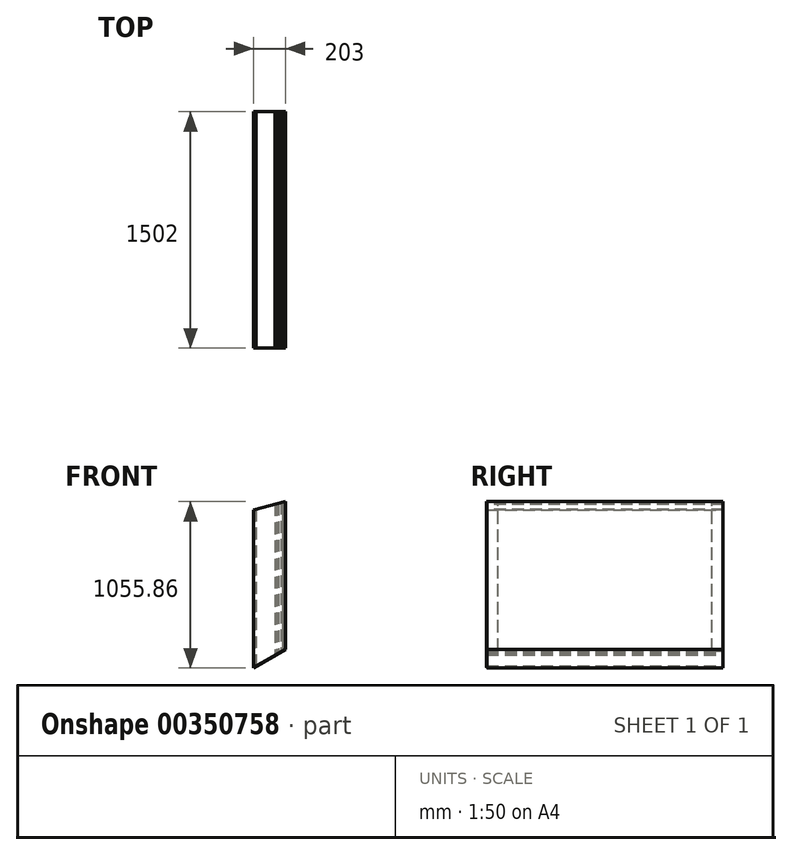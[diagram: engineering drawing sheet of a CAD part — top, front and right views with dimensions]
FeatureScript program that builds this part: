
annotation { "Feature Type Name" : "Feature", "Feature Type Description" : "" }
export const myFeature = defineFeature(function(context is Context, id is Id, definition is map)
    precondition{}
    {
        {
            var Q0;
            Q0=qCreatedBy(makeId("Right.planeOp"),FACE);
            var sketch = newSketch(context, id + "F0", { "sketchPlane" : qUnion([Q0])});
            skLineSegment(sketch, "E0", {"start": v(0, 0) * mm, "end": v(1500, 0) * mm});
            skLineSegment(sketch, "E1", {"start": v(1500, 0) * mm, "end": v(1500, 1200) * mm});
            skLineSegment(sketch, "E2", {"start": v(1500, 1200) * mm, "end": v(0, 1200) * mm});
            skLineSegment(sketch, "E3", {"start": v(0, 1200) * mm, "end": v(0, 0) * mm});
            skSolve(sketch);
        }
        {
            var Q0;
            Q0=makeQuery(id+"F0.imprint","IMPRINT",FACE,{"disambiguationData":[TD([[makeQuery(id+"F0.imprint","IMPRINT",EDGE,{"derivedFrom":sQuery(id+"F0.wireOp",EDGE,"E0")}),1.0]])]});
            extrude(context, id + "F1", {"entities" : qUnion([Q0]), "depth" : 6 * mm});
        }
        {
            var Q0;
            Q0=makeQuery(id+"F1.opExtrude","CAP_FACE",FACE,{"disambiguationData":[OSD([sQuery(id+"F0.wireOp",EDGE,"E0"),sQuery(id+"F0.wireOp",EDGE,"E1"),sQuery(id+"F0.wireOp",EDGE,"E2"),sQuery(id+"F0.wireOp",EDGE,"UxQu33BP-PdVc-IvKo-0Oal-Oq9sfbCTzBfW"),sQuery(id+"F0.wireOp",EDGE,"E3")])],"isStart":false});
            extrude(context, id + "F2", {"entities" : qUnion([Q0]), "depth" : 1 * mm});
        }
        {
            var Q0;
            Q0=makeQuery(id+"F2.opExtrude","CAP_FACE",FACE,{"disambiguationData":[OSD([sQuery(id+"F0.wireOp",EDGE,"E0"),sQuery(id+"F0.wireOp",EDGE,"E1"),sQuery(id+"F0.wireOp",EDGE,"E2"),sQuery(id+"F0.wireOp",EDGE,"UxQu33BP-PdVc-IvKo-0Oal-Oq9sfbCTzBfW"),sQuery(id+"F0.wireOp",EDGE,"E3")])],"isStart":false});
            extrude(context, id + "F3", {"entities" : qUnion([Q0]), "depth" : 10 * mm});
        }
        {
            var Q0;
            Q0=makeQuery(id+"F3.opExtrude","CAP_FACE",FACE,{"disambiguationData":[OSD([sQuery(id+"F0.wireOp",EDGE,"E0"),sQuery(id+"F0.wireOp",EDGE,"E1"),sQuery(id+"F0.wireOp",EDGE,"E2"),sQuery(id+"F0.wireOp",EDGE,"UxQu33BP-PdVc-IvKo-0Oal-Oq9sfbCTzBfW"),sQuery(id+"F0.wireOp",EDGE,"E3")])],"isStart":false});
            extrude(context, id + "F4", {"entities" : qUnion([Q0]), "depth" : 120 * mm});
        }
        {
            var Q0;
            Q0=makeQuery(id+"F4.opExtrude","CAP_FACE",FACE,{"disambiguationData":[OSD([sQuery(id+"F0.wireOp",EDGE,"E0"),sQuery(id+"F0.wireOp",EDGE,"E1"),sQuery(id+"F0.wireOp",EDGE,"E2"),sQuery(id+"F0.wireOp",EDGE,"UxQu33BP-PdVc-IvKo-0Oal-Oq9sfbCTzBfW"),sQuery(id+"F0.wireOp",EDGE,"E3")])],"isStart":false});
            extrude(context, id + "F5", {"entities" : qUnion([Q0]), "depth" : 10 * mm});
        }
        {
            var Q0;
            Q0=makeQuery(id+"F5.opExtrude","CAP_FACE",FACE,{"disambiguationData":[OSD([sQuery(id+"F0.wireOp",EDGE,"E0"),sQuery(id+"F0.wireOp",EDGE,"E1"),sQuery(id+"F0.wireOp",EDGE,"E2"),sQuery(id+"F0.wireOp",EDGE,"UxQu33BP-PdVc-IvKo-0Oal-Oq9sfbCTzBfW"),sQuery(id+"F0.wireOp",EDGE,"E3")])],"isStart":false});
            extrude(context, id + "F6", {"entities" : qUnion([Q0]), "depth" : 10 * mm});
        }
        {
            var Q0;
            Q0=makeQuery(id+"F6.opExtrude","CAP_FACE",FACE,{"disambiguationData":[OSD([sQuery(id+"F0.wireOp",EDGE,"E0"),sQuery(id+"F0.wireOp",EDGE,"E1"),sQuery(id+"F0.wireOp",EDGE,"E2"),sQuery(id+"F0.wireOp",EDGE,"UxQu33BP-PdVc-IvKo-0Oal-Oq9sfbCTzBfW"),sQuery(id+"F0.wireOp",EDGE,"E3")])],"isStart":false});
            extrude(context, id + "F7", {"entities" : qUnion([Q0]), "depth" : 18 * mm});
        }
        {
            var Q0;
            Q0=makeQuery(id+"F7.opExtrude","CAP_FACE",FACE,{"disambiguationData":[OSD([sQuery(id+"F0.wireOp",EDGE,"E0"),sQuery(id+"F0.wireOp",EDGE,"E1"),sQuery(id+"F0.wireOp",EDGE,"E2"),sQuery(id+"F0.wireOp",EDGE,"UxQu33BP-PdVc-IvKo-0Oal-Oq9sfbCTzBfW"),sQuery(id+"F0.wireOp",EDGE,"E3")])],"isStart":false});
            extrude(context, id + "F8", {"entities" : qUnion([Q0]), "depth" : 10 * mm});
        }
        {
            var Q0;
            Q0=makeQuery(id+"F8.opExtrude","CAP_FACE",FACE,{"disambiguationData":[OSD([sQuery(id+"F0.wireOp",EDGE,"E0"),sQuery(id+"F0.wireOp",EDGE,"E1"),sQuery(id+"F0.wireOp",EDGE,"E2"),sQuery(id+"F0.wireOp",EDGE,"E3")])],"isStart":false});
            extrude(context, id + "F9", {"entities" : qUnion([Q0]), "depth" : 1 * mm});
        }
        {
            var Q0;
            Q0=makeQuery(id+"F9.opExtrude","CAP_FACE",FACE,{"disambiguationData":[OSD([sQuery(id+"F0.wireOp",EDGE,"E0"),sQuery(id+"F0.wireOp",EDGE,"E1"),sQuery(id+"F0.wireOp",EDGE,"E2"),sQuery(id+"F0.wireOp",EDGE,"E3")])],"isStart":false});
            var sketch = newSketch(context, id + "F10", { "sketchPlane" : qUnion([Q0])});
            skLineSegment(sketch, "E4.bottom", {"start": v(0, 0) * mm, "end": v(70, 0) * mm});
            skLineSegment(sketch, "E4.top", {"start": v(0, 1200) * mm, "end": v(70, 1200) * mm});
            skLineSegment(sketch, "E4.left", {"start": v(0, 0) * mm, "end": v(0, 1200) * mm});
            skLineSegment(sketch, "E4.right", {"start": v(70, 0) * mm, "end": v(70, 1200) * mm});
            skLineSegment(sketch, "E5.bottom", {"start": v(1500, 0) * mm, "end": v(1430, 0) * mm});
            skLineSegment(sketch, "E5.top", {"start": v(1500, 1200) * mm, "end": v(1430, 1200) * mm});
            skLineSegment(sketch, "E5.left", {"start": v(1500, 0) * mm, "end": v(1500, 1200) * mm});
            skLineSegment(sketch, "E5.right", {"start": v(1430, 0) * mm, "end": v(1430, 1200) * mm});
            skSolve(sketch);
        }
        {
            var Q0;
            Q0=qSketchRegion(id+"F10",true);
            extrude(context, id + "F11", {"entities" : qUnion([Q0]), "depth" : 8 * mm});
        }
        {
            var Q0;
            Q0=makeQuery(id+"F11.opExtrude","CAP_FACE",FACE,{"disambiguationData":[OSD([sQuery(id+"F10.wireOp",EDGE,"E4.bottom"),sQuery(id+"F10.wireOp",EDGE,"E4.top"),sQuery(id+"F10.wireOp",EDGE,"E4.left"),sQuery(id+"F10.wireOp",EDGE,"E4.right")])],"isStart":false});
            var sketch = newSketch(context, id + "F12", { "sketchPlane" : qUnion([Q0])});
            skLineSegment(sketch, "E6.bottom", {"start": v(0, 0) * mm, "end": v(1500, 0) * mm});
            skLineSegment(sketch, "E6.top", {"start": v(0, 1200) * mm, "end": v(1500, 1200) * mm});
            skLineSegment(sketch, "E6.left", {"start": v(0, 0) * mm, "end": v(0, 1200) * mm});
            skLineSegment(sketch, "E6.right", {"start": v(1500, 0) * mm, "end": v(1500, 1200) * mm});
            skSolve(sketch);
        }
        {
            var Q0;
            Q0=qSketchRegion(id+"F12",true);
            extrude(context, id + "F13", {"entities" : qUnion([Q0]), "depth" : 8 * mm});
        }
        {
            var Q0;
            Q0=makeQuery(id+"F4.opExtrude","SWEPT_FACE",FACE,{"disambiguationData":[OSD([sQuery(id+"F0.wireOp",EDGE,"E3")])]});
            var sketch = newSketch(context, id + "F14", { "sketchPlane" : qUnion([Q0])});
            skLineSegment(sketch, "E7.bottom", {"start": v(202, 0) * mm, "end": v(0, 0) * mm});
            skLineSegment(sketch, "E7.top", {"start": v(202, 1200) * mm, "end": v(0, 1200) * mm});
            skLineSegment(sketch, "E7.left", {"start": v(202, 0) * mm, "end": v(202, 1200) * mm});
            skLineSegment(sketch, "E7.right", {"start": v(0, 0) * mm, "end": v(0, 1200) * mm});
            skSolve(sketch);
        }
        {
            var Q0;
            Q0 = qSketchRegion(id + "F14", true);
            extrude(context, id + "F15", {"entities" : qUnion([Q0]), "depth" : 2 * mm});
        }
        {
            var Q0;
            Q0=makeQuery(id+"F4.opExtrude","SWEPT_FACE",FACE,{"disambiguationData":[OSD([sQuery(id+"F0.wireOp",EDGE,"E1")])]});
            var sketch = newSketch(context, id + "F16", { "sketchPlane" : qUnion([Q0])});
            skLineSegment(sketch, "E8", {"start": v(0, 0) * mm, "end": v(-202, 0) * mm});
            skLineSegment(sketch, "E9", {"start": v(-202, 0) * mm, "end": v(-202, 116.62) * mm});
            skLineSegment(sketch, "E10", {"start": v(-202, 116.62) * mm, "end": v(0, 0) * mm});
            skLineSegment(sketch, "E11", {"start": v(0, 1200) * mm, "end": v(0, 1000) * mm});
            skLineSegment(sketch, "E12", {"start": v(0, 1000) * mm, "end": v(-202, 1054.13) * mm});
            skLineSegment(sketch, "E13", {"start": v(-202, 1054.13) * mm, "end": v(-202, 1200) * mm});
            skLineSegment(sketch, "E14", {"start": v(-202, 1200) * mm, "end": v(0, 1200) * mm});
            skSolve(sketch);
        }
        {
            var Q0;
            Q0 = qSketchRegion(id + "F16", true);
            extrude(context, id + "F17", {"entities" : qUnion([Q0]), "operationType" : NewBodyOperationType.REMOVE, "endBound" : BoundingType.THROUGH_ALL, "oppositeDirection" : true, "depth" : 25 * mm});
        }
        {
            var Q0;
            {var subQ0=sQuery(id+"F0.wireOp",EDGE,"E1");Q0=makeQuery(id+"F17.boolean.opBoolean","COPY",FACE,{"disambiguationData":[TD([makeQuery(id+"F4.opExtrude","SWEPT_FACE",FACE,{"disambiguationData":[OSD([subQ0])]})])],"derivedFrom":makeQuery(id+"F17.opExtrude","SWEPT_FACE",FACE,{"disambiguationData":[OSD([sQuery(id+"F16.wireOp",EDGE,"E10")])]})});}
            var sketch = newSketch(context, id + "F18", { "sketchPlane" : qUnion([Q0])});
            skLineSegment(sketch, "E15.bottom", {"start": v(0, 0) * mm, "end": v(233.25, 0) * mm});
            skLineSegment(sketch, "E15.top", {"start": v(0, -1500) * mm, "end": v(233.25, -1500) * mm});
            skLineSegment(sketch, "E15.left", {"start": v(0, 0) * mm, "end": v(0, -1500) * mm});
            skLineSegment(sketch, "E15.right", {"start": v(233.25, 0) * mm, "end": v(233.25, -1500) * mm});
            skSolve(sketch);
        }
        {
            var Q0;
            Q0 = qSketchRegion(id + "F18", true);
            extrude(context, id + "F19", {"entities" : qUnion([Q0]), "depth" : 2 * mm});
        }
    });
